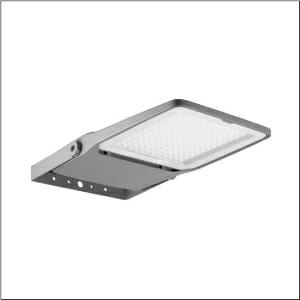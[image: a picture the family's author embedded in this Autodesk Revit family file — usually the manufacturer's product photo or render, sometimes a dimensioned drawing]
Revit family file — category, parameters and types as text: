
# Revit family: floodlight_fl_20_midi___pl52_5xa7682e2d2ac_72a0
name_source: partatom
category: Lighting Fixtures
units: mm (PartAtom-declared; Revit-internal decimal feet)

## family parameters
Cut with Voids When Loaded = No
Host = Face
Light Source = No
Part Type = Normal
Room Calculation Point = No
Round Connector Dimension = Use Diameter
Shared = No

## types (1)
- --- (1 x LED 4000K / CRI = 70 (unbekannt), 26840 lm, 4000K)
    Apparent Load = 208 VA
    CIE Flux Codes = 27 59 98 100 100
    Color Rendering = 70
    Color Temperature = 4000K
    Default Elevation = 1800 mm
    Description = Floodlight FL 20 midi, floodlight, primary light control with lens, of plastic, primary optical cover: protective disc, of toughened safety glass, transparent, light distribution: PL52, light emission: direct distribution, primary light characteristic: asymmetric, installation type: surface-mounted, LED, High Power LED, rated luminous flux: 26.840lm, luminous efficacy: 129lm/W, light colour: 740, colour temperature: 4000K, control gear: ECG Plus, control: flexible luminous flux parameterisation, time-dependent luminous flux control, digital communication interface, power reduction, overheat protection, electronic power reduction, with terminal, 5-pole, max. 2.5mm², mains connection: 220..240V, AC, 50/60Hz, rated input power: 208W, LED unit, of diecast aluminium, powder-coated, Siteco® metallic grey (DB 702S), corrosivity category C5 mid according to DIN EN ISO 12944, incl. 1x M20 cable gland for cable Ø 6.5..12mm, length: 731mm, width: 450mm, height: 76mm, housing frame, of diecast aluminium, powder-coated, Siteco® metallic grey (DB 702S), wall fastening, of steel, powder-coated, Siteco® metallic grey (DB 702S), DALI, protection rating (complete): IP66, insulation class (complete): insulation class II (safety insulation), certification: CE, ENEC, VDE, protection symbol: D, permissible operating ambient temperature: -40..+40°C, permissible operating ambient temperature for outdoor applications: -40..+50°C, standard: DIN EN 12944, packaging unit: 1 piece

Light Distribution: PL52
    Height = 76 mm
    Lamp = 1 x LED 4000K / CRI >= 70 (unbekannt)
    Lamp Light Flux = 26840 lm
    Lamp count = 1
    Length = 731 mm
    Luminous efficacy = 129 lm/W
    Manufacturer = Siteco
    ModVariant = No
    Model = 5XA7682E2D2AC
    Mounting Place = Wall
    Mounting Type = Surface mounted
    Number of Poles = 1
    OnlyDefault = Yes
    Power Factor = 1
    Product Name = Floodlight FL 20 midi | PL52
    Product group = floodlight | wall mounted
    ProductGroupID = 2001
    Protection Class = Protection class II
    Protection Degree = IP 66
    RLX_Detail_Level = 1
    RLX_Emergency_Light_Flux = 0 lm
    RLX_Emergency_Type = 0
    RLX_Emergency_Type_DB = No
    RlxData = <blob elided: 92249 chars, md5=f9ff8d6a>
    Socket = socket
    Standby Power = 0 W
    System Light Flux = 26840 lm
    System Power = 208 W
    Type Comments = factory setting: luminous flux: 100 % | dim-lin: 254 | 484 mA
    Type Image = l_1005944.jpg
    URL = http://relux.com
    VarID = @adj_147569
    Voltage = 0 V
    Weight = 0.00 kg
    Width = 450 mm

## geometry (parser evidence)
native form markers: Blend x4, Sweep x13
no freeform markers — native parametric forms only
